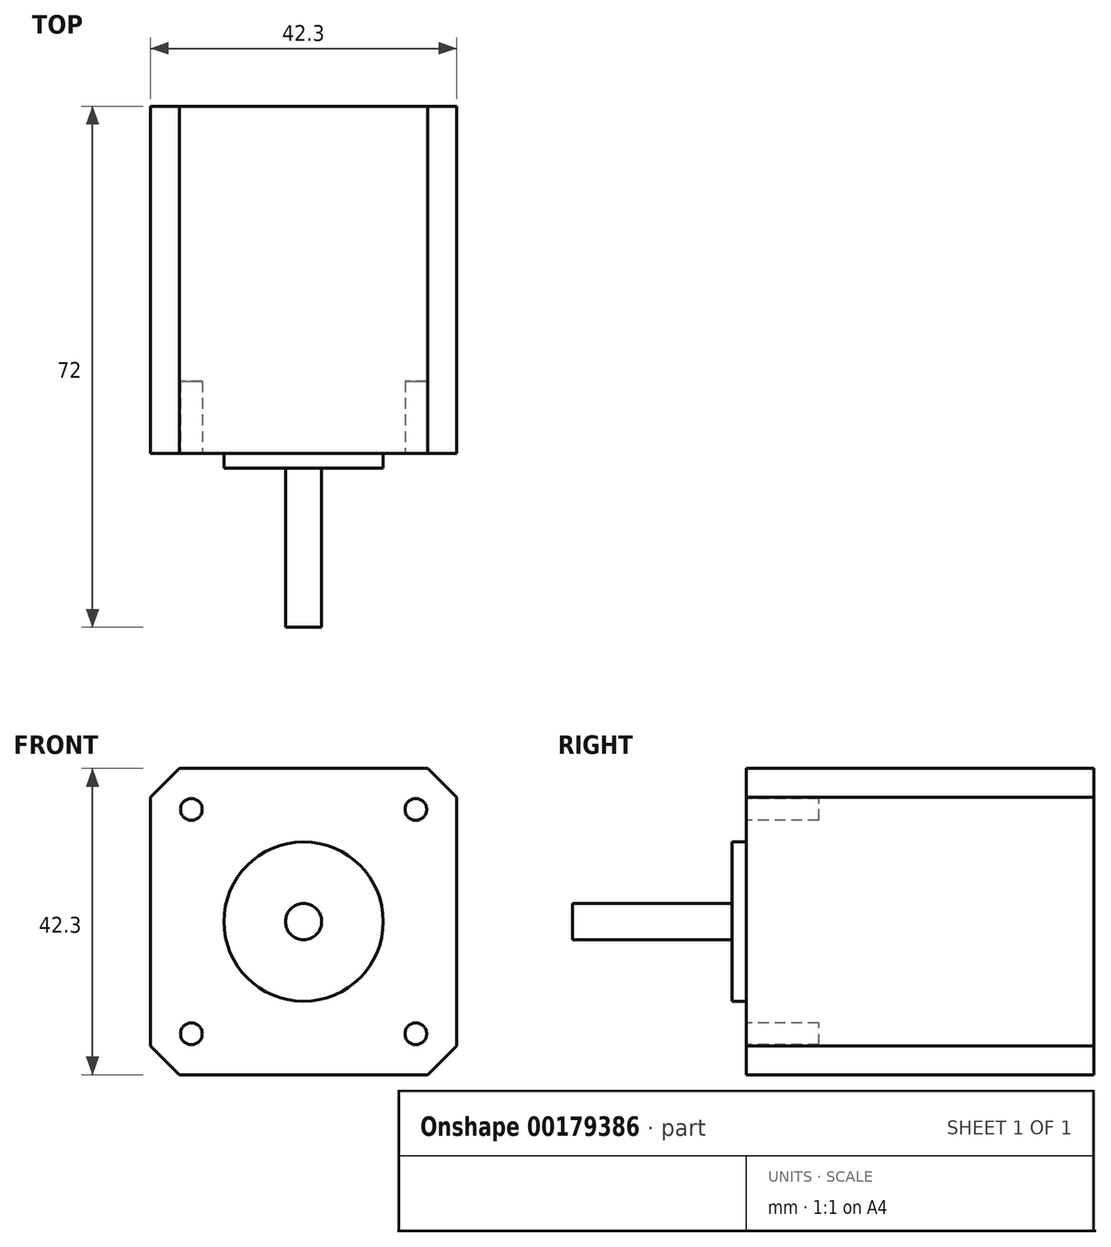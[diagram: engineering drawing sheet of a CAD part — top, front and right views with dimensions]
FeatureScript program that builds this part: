
annotation { "Feature Type Name" : "Feature", "Feature Type Description" : "" }
export const myFeature = defineFeature(function(context is Context, id is Id, definition is map)
    precondition{}
    {
        {
            var Q0;
            Q0=qCreatedBy(makeId("Front.planeOp"),FACE);
            var sketch = newSketch(context, id + "F0", { "sketchPlane" : qUnion([Q0])});
            skLineSegment(sketch, "E0.bottom", {"start": v(0, 0) * mm, "end": v(-21.15, 0) * mm, "construction": true});
            skLineSegment(sketch, "E0.top", {"start": v(0, 21.15) * mm, "end": v(-17.15, 21.15) * mm});
            skLineSegment(sketch, "E0.left", {"start": v(0, 0) * mm, "end": v(0, 21.15) * mm, "construction": true});
            skLineSegment(sketch, "E0.right", {"start": v(-21.15, 0) * mm, "end": v(-21.15, 17.15) * mm});
            skLineSegment(sketch, "E1", {"start": v(-17.15, 21.15) * mm, "end": v(-21.15, 17.15) * mm});
            skPoint(sketch, "E2.orphan", {"position": v(-21.15, 21.15) * mm});
            skLineSegment(sketch, "E3.MirrorCS", {"start": v(17.15, 21.15) * mm, "end": v(21.15, 17.15) * mm});
            skLineSegment(sketch, "E4.MirrorCS", {"start": v(21.15, 0) * mm, "end": v(21.15, 17.15) * mm});
            skLineSegment(sketch, "E5.MirrorCS", {"start": v(0, 21.15) * mm, "end": v(17.15, 21.15) * mm});
            skLineSegment(sketch, "E6.MirrorCS", {"start": v(-21.15, 0) * mm, "end": v(-21.15, -17.15) * mm});
            skLineSegment(sketch, "E7.MirrorCS", {"start": v(-17.15, -21.15) * mm, "end": v(-21.15, -17.15) * mm});
            skLineSegment(sketch, "E8.MirrorCS", {"start": v(0, -21.15) * mm, "end": v(-17.15, -21.15) * mm});
            skLineSegment(sketch, "E9.MirrorCS", {"start": v(0, -21.15) * mm, "end": v(17.15, -21.15) * mm});
            skLineSegment(sketch, "E10.MirrorCS", {"start": v(17.15, -21.15) * mm, "end": v(21.15, -17.15) * mm});
            skLineSegment(sketch, "E11.MirrorCS", {"start": v(21.15, 0) * mm, "end": v(21.15, -17.15) * mm});
            skSolve(sketch);
        }
        {
            var Q0;
            Q0 = qSketchRegion(id + "F0", true);
            extrude(context, id + "F1", {"entities" : qUnion([Q0]), "depth" : 48 * mm});
        }
        {
            var Q0;
            Q0=makeQuery(id+"F1.opExtrude","CAP_FACE",FACE,{"disambiguationData":[OSD([sQuery(id+"F0.wireOp",EDGE,"E0.top"),sQuery(id+"F0.wireOp",EDGE,"E0.right"),sQuery(id+"F0.wireOp",EDGE,"E1"),sQuery(id+"F0.wireOp",EDGE,"E3.MirrorCS"),sQuery(id+"F0.wireOp",EDGE,"E4.MirrorCS"),sQuery(id+"F0.wireOp",EDGE,"E5.MirrorCS"),sQuery(id+"F0.wireOp",EDGE,"E6.MirrorCS"),sQuery(id+"F0.wireOp",EDGE,"E7.MirrorCS"),sQuery(id+"F0.wireOp",EDGE,"E8.MirrorCS"),sQuery(id+"F0.wireOp",EDGE,"E9.MirrorCS"),sQuery(id+"F0.wireOp",EDGE,"E10.MirrorCS"),sQuery(id+"F0.wireOp",EDGE,"E11.MirrorCS")])],"isStart":false});
            var sketch = newSketch(context, id + "F2", { "sketchPlane" : qUnion([Q0])});
            skCircle(sketch, "E12", {"center": v(0, 0) * mm, "radius": 11 * mm});
            skSolve(sketch);
        }
        {
            var Q0;
            Q0=makeQuery(id+"F2.imprint","IMPRINT",FACE,{"disambiguationData":[TD([[makeQuery(id+"F2.imprint","IMPRINT",EDGE,{"derivedFrom":sQuery(id+"F2.wireOp",EDGE,"E12")}),1.0]])]});
            extrude(context, id + "F3", {"entities" : qUnion([Q0]), "operationType" : NewBodyOperationType.ADD, "depth" : 2 * mm});
        }
        {
            var Q0;
            Q0=makeQuery(id+"F3.opExtrude","CAP_FACE",FACE,{"disambiguationData":[OSD([sQuery(id+"F2.wireOp",EDGE,"E12")])],"isStart":false});
            var sketch = newSketch(context, id + "F4", { "sketchPlane" : qUnion([Q0])});
            skCircle(sketch, "E13", {"center": v(0, 0) * mm, "radius": 2.5 * mm});
            skSolve(sketch);
        }
        {
            var Q0;
            Q0 = qSketchRegion(id + "F4", true);
            extrude(context, id + "F5", {"entities" : qUnion([Q0]), "operationType" : NewBodyOperationType.ADD, "depth" : 22 * mm});
        }
        {
            var Q0;
            Q0=makeQuery(id+"F1.opExtrude","CAP_FACE",FACE,{"disambiguationData":[OSD([sQuery(id+"F0.wireOp",EDGE,"E0.top"),sQuery(id+"F0.wireOp",EDGE,"E0.right"),sQuery(id+"F0.wireOp",EDGE,"E1"),sQuery(id+"F0.wireOp",EDGE,"E3.MirrorCS"),sQuery(id+"F0.wireOp",EDGE,"E4.MirrorCS"),sQuery(id+"F0.wireOp",EDGE,"E5.MirrorCS"),sQuery(id+"F0.wireOp",EDGE,"E6.MirrorCS"),sQuery(id+"F0.wireOp",EDGE,"E7.MirrorCS"),sQuery(id+"F0.wireOp",EDGE,"E8.MirrorCS"),sQuery(id+"F0.wireOp",EDGE,"E9.MirrorCS"),sQuery(id+"F0.wireOp",EDGE,"E10.MirrorCS"),sQuery(id+"F0.wireOp",EDGE,"E11.MirrorCS")])],"isStart":false});
            var sketch = newSketch(context, id + "F6", { "sketchPlane" : qUnion([Q0])});
            skLineSegment(sketch, "E14.bottom", {"start": v(-15.5, -15.5) * mm, "end": v(15.5, -15.5) * mm, "construction": true});
            skLineSegment(sketch, "E14.top", {"start": v(-15.5, 15.5) * mm, "end": v(15.5, 15.5) * mm, "construction": true});
            skLineSegment(sketch, "E14.left", {"start": v(-15.5, -15.5) * mm, "end": v(-15.5, 15.5) * mm, "construction": true});
            skLineSegment(sketch, "E14.right", {"start": v(15.5, -15.5) * mm, "end": v(15.5, 15.5) * mm, "construction": true});
            skPoint(sketch, "E14.middle", {"position": v(0, 0) * mm});
            skCircle(sketch, "E15", {"center": v(-15.5, 15.5) * mm, "radius": 1.5 * mm});
            skCircle(sketch, "E16", {"center": v(15.5, 15.5) * mm, "radius": 1.5 * mm});
            skCircle(sketch, "E17", {"center": v(-15.5, -15.5) * mm, "radius": 1.5 * mm});
            skCircle(sketch, "E18", {"center": v(15.5, -15.5) * mm, "radius": 1.5 * mm});
            skSolve(sketch);
        }
        {
            var Q0;
            Q0 = qSketchRegion(id + "F6", true);
            extrude(context, id + "F7", {"entities" : qUnion([Q0]), "operationType" : NewBodyOperationType.REMOVE, "oppositeDirection" : true, "depth" : 10 * mm});
        }
    });
